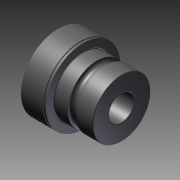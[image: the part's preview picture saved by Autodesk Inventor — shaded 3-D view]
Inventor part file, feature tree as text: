
AUTODESK INVENTOR PART (.ipt)
format: ipt  version: 2016 (Build 200138000, 138)  size: 231,936 bytes
history: native  units: mm
features: other x7, revolve x1, sketch x1
ambient origin geometry x8: Origin, YZ Plane, XZ Plane, XY Plane, X Axis, Y Axis, Z Axis, Center Point
bodies: Solid1 (feature_tree)
feature tree (9):
  revolve  "Revolution1"  [1 undecoded]
  other  "to_housing_XY"
  other  "to_housing_YZ"
  other  "to_housing_ZX"
  other  "to_housing_X"
  other  "to_housing_Y"
  other  "to_housing_Z"
  other  "to_housing_Center"
  sketch  "Sketch_1"  dims[d0=360.0deg d1=0.0mm]
note: 1 required parameter value undecoded (feature->parameter linkage not recoverable at this tier; creation-order binding heuristic only, values carry confidence <= 0.55)
